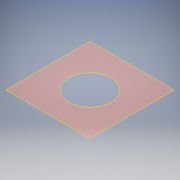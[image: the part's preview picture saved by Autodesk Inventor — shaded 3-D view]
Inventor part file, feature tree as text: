
AUTODESK INVENTOR PART (.ipt)
format: ipt  version: 2018 (Build 220112000, 112)  size: 93,696 bytes
history: native  units: mm
features: sketch x1, other x1, surface_op x1
ambient origin geometry x8: Origin, YZ Plane, XZ Plane, XY Plane, X Axis, Y Axis, Z Axis, Center Point
bodies: Body1 (feature_tree)
feature tree (3):
  sketch  "Sketch1"  dims[d0=30.0mm d1=30.0mm d2=15.0mm d3=15.0mm d4=15.0mm]
  other  "Srf1"
  surface_op  "Boundary Patch1"
